# Revit family: Reece_Shower_Milli_Inox_Handpiece
name_source: partatom
category: Plumbing Fixtures
revit_build: Autodesk Revit 2018 (Build: 20190510_1515(x64)
units: mm (PartAtom-declared; Revit-internal decimal feet)

## family parameters
Cut with Voids When Loaded = No
Host = Face
Part Type = Normal
Room Calculation Point = Yes
Round Connector Dimension = Use Diameter
Shared = Yes

## types (1)
- Brushed Stainless Steel
    CWFU = 0
    Default Elevation = 1000 mm
    Description = Milli Inox Shower Handpiece Only Stainless Steel
    Disclaimer = THIS FILE IS THE PROPERTY OF THE REECE GROUP. IT MAY NOT BE REPRODUCED, REVERSE-ENGINEERED OR MODIFIED. ANY REPUBLICATION, TRANSMISSION OR DISTRIBUTION FOR THE PURPOSE OF COMMERCIALLY EXPLOITING THE FILES IS PROHIBITED.
    HWFU = 0
    Keynote = Product #2259929, Reece_Shower_Milli_Inox_Handpiece - Brushed Stainless Steel
    Manufacturer = Milli
    Model = Inox
    Reece_Detail_Additional = Handpiece
    Reece_Detail_Disclaimer = THIS FILE IS THE PROPERTY OF THE REECE GROUP. IT MAY NOT BE REPRODUCED, REVERSE-ENGINEERED OR MODIFIED. ANY REPUBLICATION, TRANSMISSION OR DISTRIBUTION FOR THE PURPOSE OF COMMERCIALLY EXPLOITING THE FILES IS PROHIBITED.
    Reece_Material-Main = Reece_Brass_Brushed Stainless Steel
    Reece_Overall_Height = 185 mm
    Reece_Product_Brand = Milli
    Reece_Product_Description = Milli Inox Shower Handpiece Only Stainless Steel
    Reece_Product_Number = 2259929
    Reece_Product_Sub Brand = Inox
    Reece_Product_Type = Shower
    Reece_Product_Web Page = https://www.reece.com.au
    Reece_Tap_Inlet = 15 mm
    Type Comments = Shower
    URL = https://www.reece.com.au
    WFU = 0

## geometry (parser evidence)
native form markers: Sweep x2
no freeform markers — native parametric forms only
